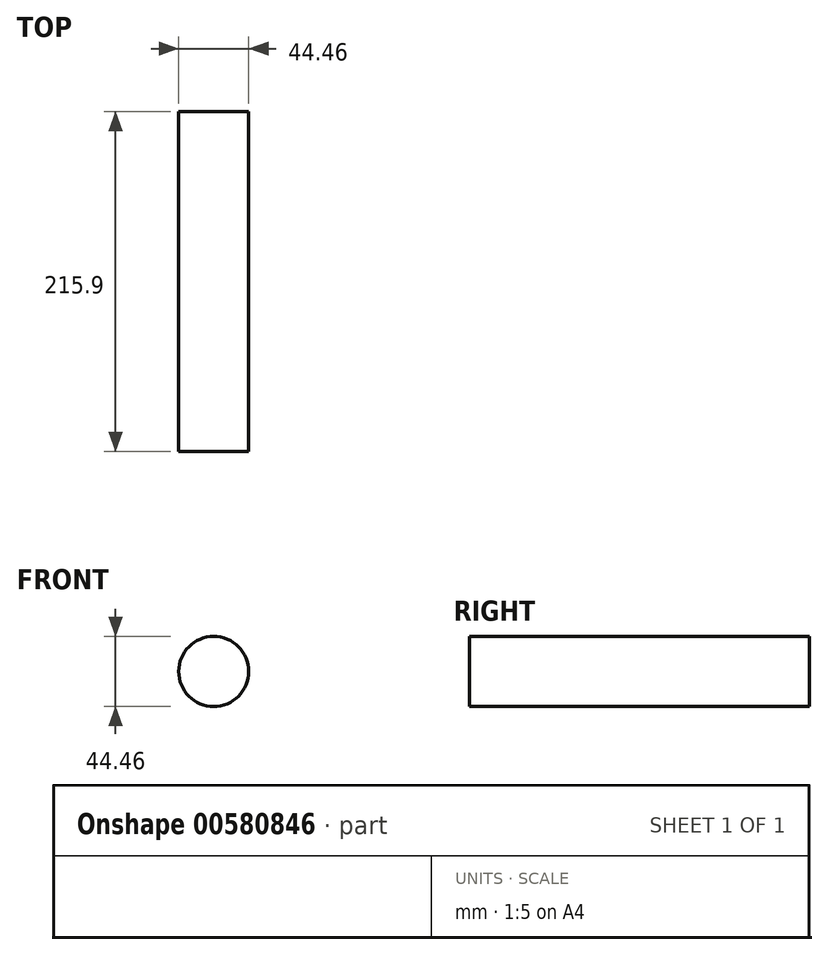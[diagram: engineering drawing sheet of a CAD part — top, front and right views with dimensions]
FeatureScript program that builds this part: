
annotation { "Feature Type Name" : "Feature", "Feature Type Description" : "" }
export const myFeature = defineFeature(function(context is Context, id is Id, definition is map)
    precondition{}
    {
        {
            var Q0;
            Q0=qCreatedBy(makeId("Front.planeOp"),FACE);
            var sketch = newSketch(context, id + "F0", { "sketchPlane" : qUnion([Q0])});
            skCircle(sketch, "E0", {"center": v(0, 0) * mm, "radius": 22.23 * mm});
            skSolve(sketch);
        }
        {
            var Q0;
            Q0 = qSketchRegion(id + "F0", true);
            extrude(context, id + "F1", {"entities" : qUnion([Q0]), "depth" : 215.9 * mm, "offsetDistance" : 25.4 * mm});
        }
    });
